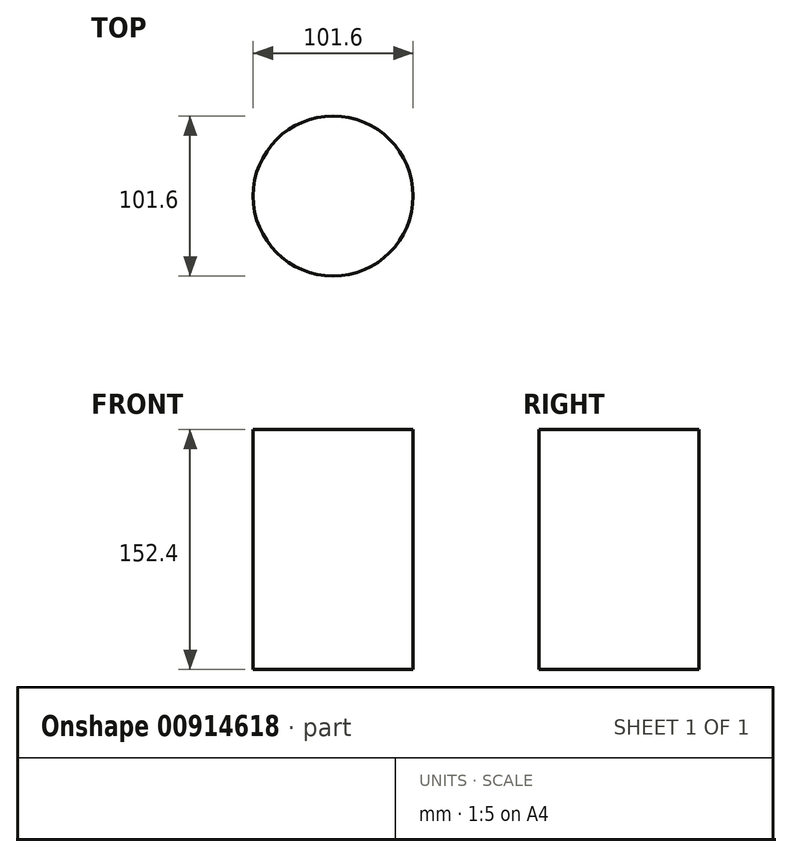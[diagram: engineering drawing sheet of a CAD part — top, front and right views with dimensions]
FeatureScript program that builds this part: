
annotation { "Feature Type Name" : "Feature", "Feature Type Description" : "" }
export const myFeature = defineFeature(function(context is Context, id is Id, definition is map)
    precondition{}
    {
        {
            var Q0;
            Q0=qCreatedBy(makeId("Top.planeOp"),FACE);
            var sketch = newSketch(context, id + "F0", { "sketchPlane" : qUnion([Q0])});
            skCircle(sketch, "E0", {"center": v(0, 0) * mm, "radius": 50.8 * mm});
            skSolve(sketch);
        }
        {
            var Q0;
            Q0 = qSketchRegion(id + "F0", true);
            extrude(context, id + "F1", {"entities" : qUnion([Q0]), "depth" : 152.4 * mm, "offsetDistance" : 25.4 * mm});
        }
    });
